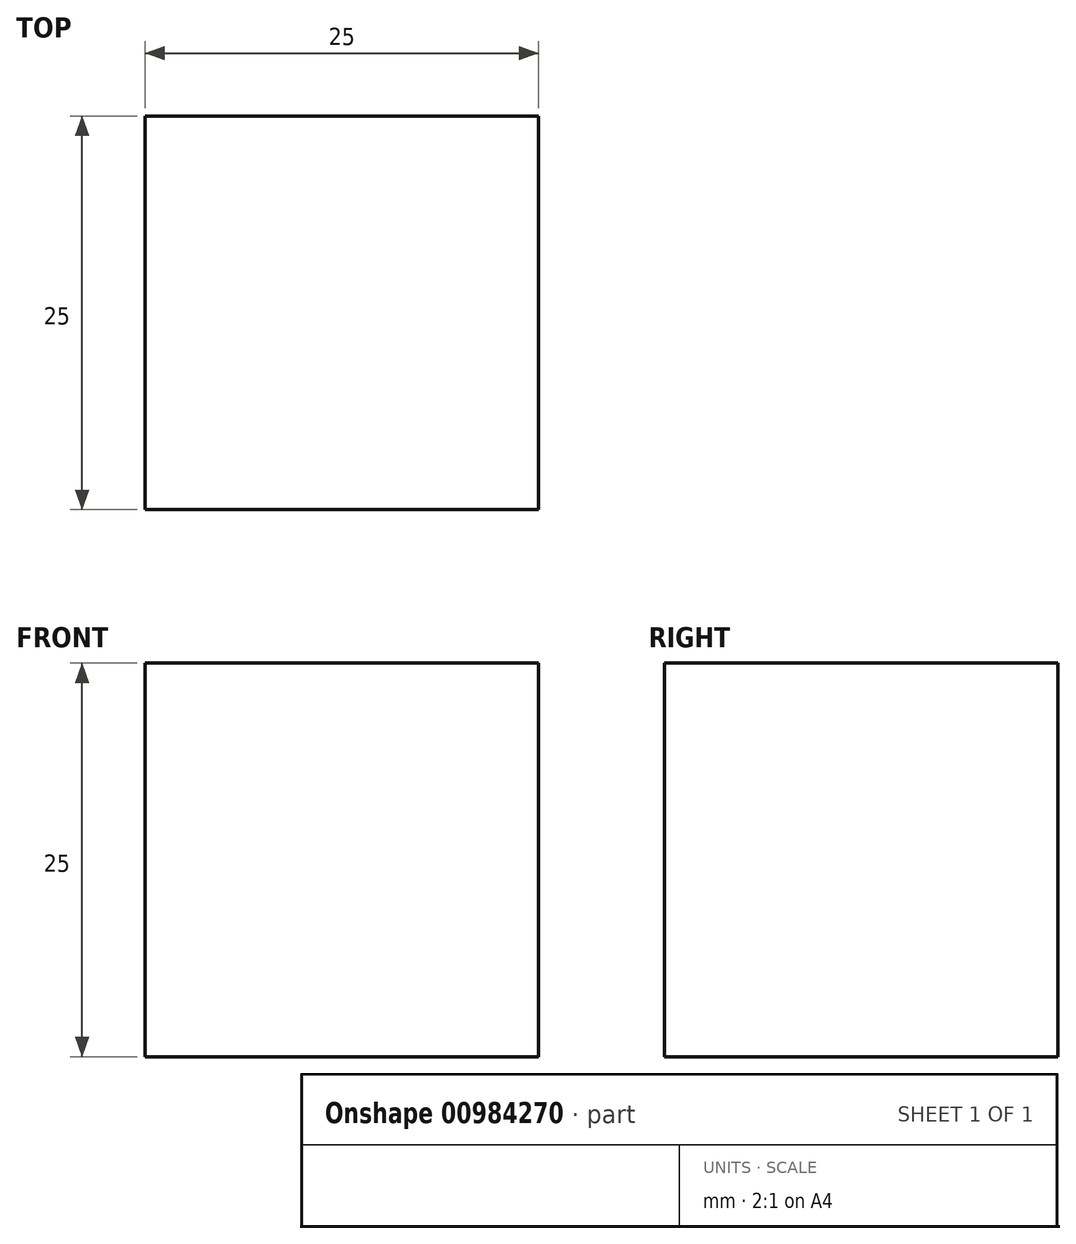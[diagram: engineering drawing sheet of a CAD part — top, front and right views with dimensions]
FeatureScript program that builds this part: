
annotation { "Feature Type Name" : "Feature", "Feature Type Description" : "" }
export const myFeature = defineFeature(function(context is Context, id is Id, definition is map)
    precondition{}
    {
        {
            var Q0;
            Q0=qCreatedBy(makeId("Top.planeOp"),FACE);
            var sketch = newSketch(context, id + "F0", { "sketchPlane" : qUnion([Q0])});
            skLineSegment(sketch, "E0.bottom", {"start": v(-9.17, 8.7) * mm, "end": v(15.83, 8.7) * mm});
            skLineSegment(sketch, "E0.top", {"start": v(-9.17, -16.3) * mm, "end": v(15.83, -16.3) * mm});
            skLineSegment(sketch, "E0.left", {"start": v(-9.17, 8.7) * mm, "end": v(-9.17, -16.3) * mm});
            skLineSegment(sketch, "E0.right", {"start": v(15.83, 8.7) * mm, "end": v(15.83, -16.3) * mm});
            skSolve(sketch);
        }
        {
            var Q0;
            Q0=makeQuery(id+"F0.imprint","IMPRINT",FACE,{"disambiguationData":[TD([[makeQuery(id+"F0.imprint","IMPRINT",EDGE,{"derivedFrom":sQuery(id+"F0.wireOp",EDGE,"E0.bottom")}),-1.0]])]});
            extrude(context, id + "F1", {"entities" : qUnion([Q0]), "depth" : 25 * mm, "offsetDistance" : 25 * mm});
        }
        {
            var Q0;
            Q0=makeQuery(id+"F1.opExtrude","CAP_FACE",FACE,{"disambiguationData":[OSD([sQuery(id+"F0.wireOp",EDGE,"E0.bottom"),sQuery(id+"F0.wireOp",EDGE,"E0.top"),sQuery(id+"F0.wireOp",EDGE,"E0.left"),sQuery(id+"F0.wireOp",EDGE,"E0.right")])],"isStart":false});
            var sketch = newSketch(context, id + "F2", { "sketchPlane" : qUnion([Q0])});
            skPoint(sketch, "E1", {"position": v(-9.17, -16.3) * mm});
            skPoint(sketch, "E2", {"position": v(15.83, -16.3) * mm});
            skPoint(sketch, "E3", {"position": v(15.83, 8.7) * mm});
            skPoint(sketch, "E4", {"position": v(-9.17, 8.7) * mm});
            skSolve(sketch);
        }
        {
            var Q0;
            Q0=makeQuery(id+"F1.opExtrude","SWEPT_FACE",FACE,{"disambiguationData":[OSD([sQuery(id+"F0.wireOp",EDGE,"E0.left")])]});
            var sketch = newSketch(context, id + "F3", { "sketchPlane" : qUnion([Q0])});
            skPoint(sketch, "E5", {"position": v(16.3, 0) * mm});
            skPoint(sketch, "E6", {"position": v(-8.7, 0) * mm});
            skSolve(sketch);
        }
        {
            var Q0;
            Q0=sQuery(id+"F2.wireOp",VERTEX,"E3");
            var Q1;
            Q1=sQuery(id+"F2.wireOp",VERTEX,"E4");
            var Q2;
            Q2=sQuery(id+"F3.wireOp",VERTEX,"E5");
            cPlane(context, id + "F4", {"entities" : qUnion([Q0, Q1, Q2]), "cplaneType" : CPlaneType.THREE_POINT, "offset" : 25 * mm, "width" : 150 * mm, "height" : 150 * mm});
        }
    });
